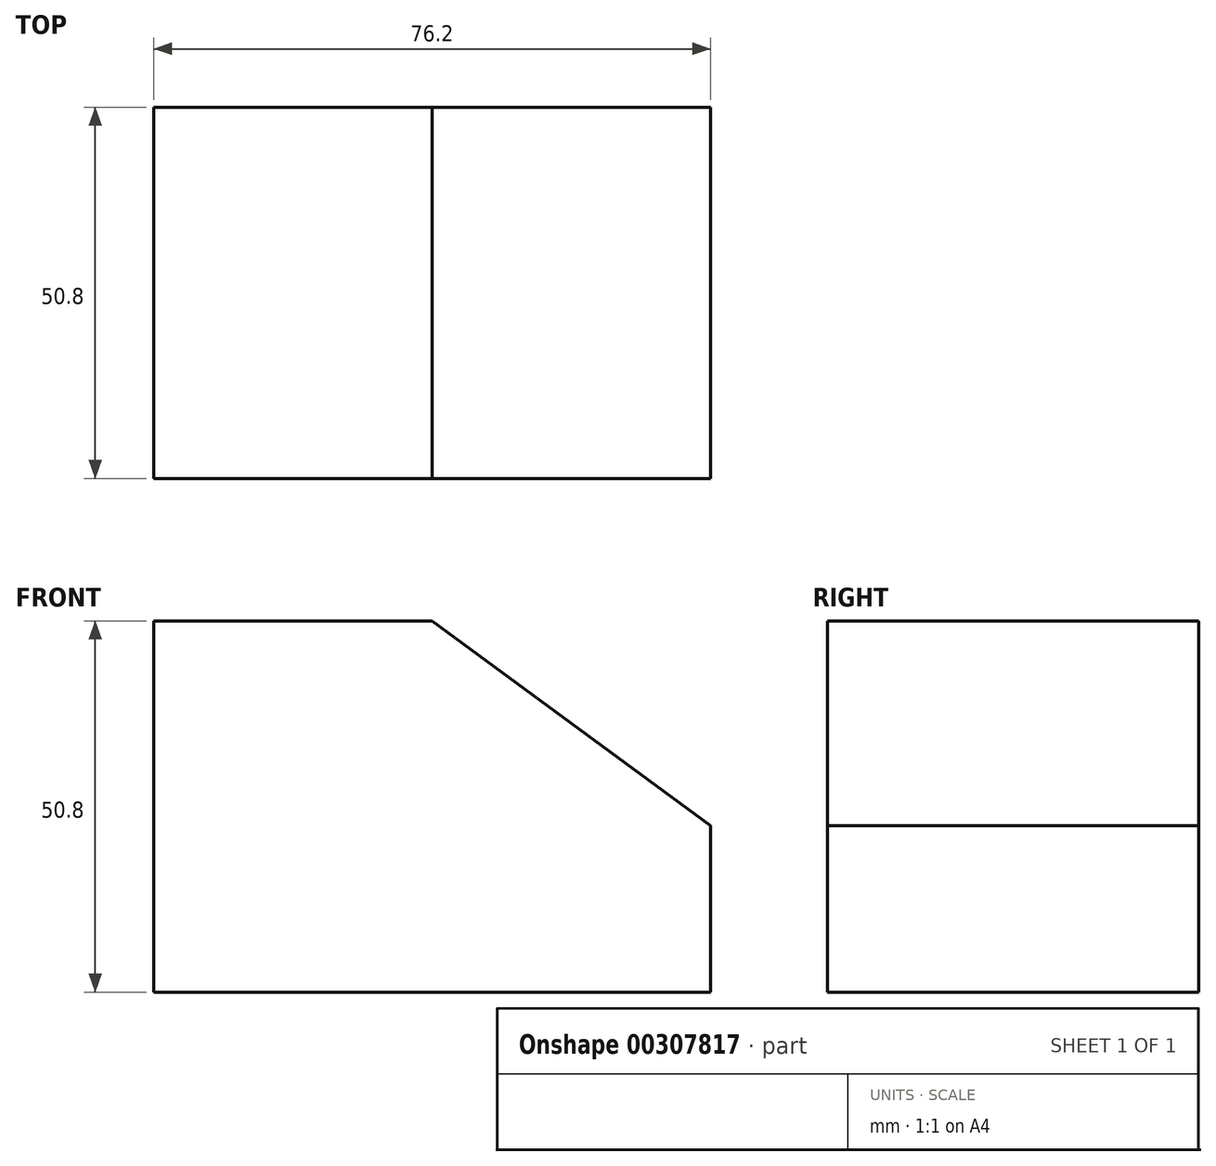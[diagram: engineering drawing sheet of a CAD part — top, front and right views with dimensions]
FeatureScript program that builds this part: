
annotation { "Feature Type Name" : "Feature", "Feature Type Description" : "" }
export const myFeature = defineFeature(function(context is Context, id is Id, definition is map)
    precondition{}
    {
        {
            var Q0;
            Q0=qCreatedBy(makeId("Front.planeOp"),FACE);
            var sketch = newSketch(context, id + "F0", { "sketchPlane" : qUnion([Q0])});
            skLineSegment(sketch, "E0", {"start": v(-26.47, -59.38) * mm, "end": v(49.73, -59.38) * mm});
            skLineSegment(sketch, "E1", {"start": v(11.63, -8.58) * mm, "end": v(-26.47, -8.58) * mm});
            skLineSegment(sketch, "E2", {"start": v(-26.47, -8.58) * mm, "end": v(-26.47, -59.38) * mm});
            skLineSegment(sketch, "E3", {"start": v(11.63, -8.58) * mm, "end": v(49.73, -36.62) * mm});
            skLineSegment(sketch, "E4", {"start": v(49.73, -36.62) * mm, "end": v(49.73, -59.38) * mm});
            skSolve(sketch);
        }
        {
            var Q0;
            Q0=makeQuery(id+"F0.imprint","IMPRINT",FACE,{"disambiguationData":[TD([[makeQuery(id+"F0.imprint","IMPRINT",EDGE,{"derivedFrom":sQuery(id+"F0.wireOp",EDGE,"E0")}),1.0]])]});
            extrude(context, id + "F1", {"entities" : qUnion([Q0]), "depth" : 50.8 * mm});
        }
    });
